# Revit family: QF_ELECTROLUXPROFESSIONAL_1LSNSP_TD6-10_G
name_source: partatom
category: Attrezzature speciali
units: mm (PartAtom-declared; Revit-internal decimal feet)

## family parameters
Basato su piano di lavoro = No
Condiviso = No
Punto di calcolo locali = No
Quota connettore circolare = Usa diametro
Sempre verticale = Sì
Taglio con vuoti quando caricato = No
Tipo di parte = Normale

## types (3) — shared parameters
Cycle = 50 Hz
Gas KW = 8
Height Actual = 1115 mm  [stored 3.65814 ft]
Latent Heat Output = 0.0
Length Actual = 720 mm  [stored 2.3622 ft]
Modello = TD6-10
Phase = 1
Produttore = Electrolux Professional
Sensible Heat Output = 0.0
URL = www.electroluxprofessional.com
Volts = 230 V
Watts = 400 W
zero-valued in all types: Prospetto di default, Steam Pounds per Hour

## per-type parameters (varying)
| type | Depth Actual | Descrizione | Item Number | Weight |
| 9873530020 | 805 mm  [stored 2.64108 ft] | TUMBLE DRYER TD6-10 10KG SST DRUM GAS 8KW 230/50/1N COMPASS PRO 6G81 SILVER/SILVER DO.RIGHT REVERSING RMC DISCON. EX... | 1LA19E | 101 |
| 9873530021 | 765 mm  [stored 2.50984 ft] | TUMBLE DRYER TD6-10 10KG GALVA.DRUM GAS 8KW 230/50/1N COMPASS PRO 6G81 SILVER/SILVER DO.RIGHT REVERSING RMC DISCON. ... | 1LSP3W | 99 |
| 9873530031 | 820 mm  [stored 2.69029 ft] | TUMBLE DRYER TD6-10 10KG GALVA.DRUM GAS GT 8KW 230/50/1N COMPASS PRO 6A81 2.I/O SILVER/SILVER DO.RIGHT ELS-NETW. PRE... | 1LA1CZ | 99 |

note: [stored X ft] marks values corroborated as IEEE doubles in the binary element streams (Revit-internal decimal feet)

## geometry (parser evidence)
native form markers: Blend x8
no freeform markers — native parametric forms only
